# Revit family: Alf Family
name_source: partatom
category: Furniture
revit_build: Autodesk Revit 2018 (Build: 20170223_1515(x64)
units: mm (PartAtom-declared; Revit-internal decimal feet)

## family parameters
Always vertical = Yes
Cut with Voids When Loaded = No
OmniClass Number = 23.40.20.00
OmniClass Title = General Furniture and Specialties
Room Calculation Point = No
Shared = No
Work Plane-Based = No

## types (13) — shared parameters

## per-type parameters (varying)
| type | Family Type |
| Stool Low (400X400X440X440) | Alf Family : Alf Low Stool (400X400X440) |
| Stool Medium (470X470X620X620) | Alf Family : Alf Medium Stool (470X470X620) |
| Stool High (470X470X800X800) | Alf Family : Alf High stool (470X470X800) |
| Stool High With Back (470X470X1020X800) | Alf Family : Alf High Stool With Back (470X470X1020) |
| Chair 3 Legs (470X540X765X440) | Alf Family : Alf Chair 3 legs (470X540X765) |
| Chair 4 Legs (470X540X765X440) | Alf Family : Alf Chair 4 Legs (470X540X765) |
| Table Round With 3 Legs (600X600X740) | Alf Family : Alf Table Round 3 Legs (600X600X740) |
| Table Round With 3 Legs (750X750X740) | Alf Family : Alf Table Round 3 legs (750X750X740) |
| Table Round With 4 Legs (750X750X740) | Alf Family : Alf Table Round 4 legs (750X750X740) |
| Table Round With 4 Legs (900X900X740) | Alf Family : Alf Table Round 4 Legs (900X900X740) |
| Table Square With 4 Legs (600X600X740) | Alf Family : Alf Table Square 4 Legs (600X600X740) |
| Table Square With 4 Legs (750X750X740) | Alf Family : Alf Table Square 4 Legs (750X750X740) |
| Table Square With 4 Legs (900X900X740) | Alf Family : Alf Table Square 4 Legs (900X900X740) |

## geometry (parser evidence)
native form markers: Sweep x75
no freeform markers — native parametric forms only
